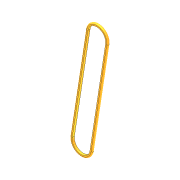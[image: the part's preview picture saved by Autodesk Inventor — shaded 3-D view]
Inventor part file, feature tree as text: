
AUTODESK INVENTOR PART (.ipt)
format: ipt  version: 2012 (Build 160160000, 160)  size: 96,256 bytes
history: native  units: in
note: dims shown in document units (in); Inventor stores cm internally (conversion verified against a paired STEP export)
features: extrude x1, fillet x1, sketch x1
ambient origin geometry x8: Origin, YZ Plane, XZ Plane, XY Plane, X Axis, Y Axis, Z Axis, Center Point
bodies: Solid1 (feature_tree)
feature tree (3):
  extrude  "Extrusion1"  Depth=0.1875in
  fillet  "Fillet1"  Radius=0.75in
  sketch  "Sketch1"  dims[d0=8.5in d1=0.1875in d2=0.75in d3=0.1875in d4=0.0in d5=0.0938in]
